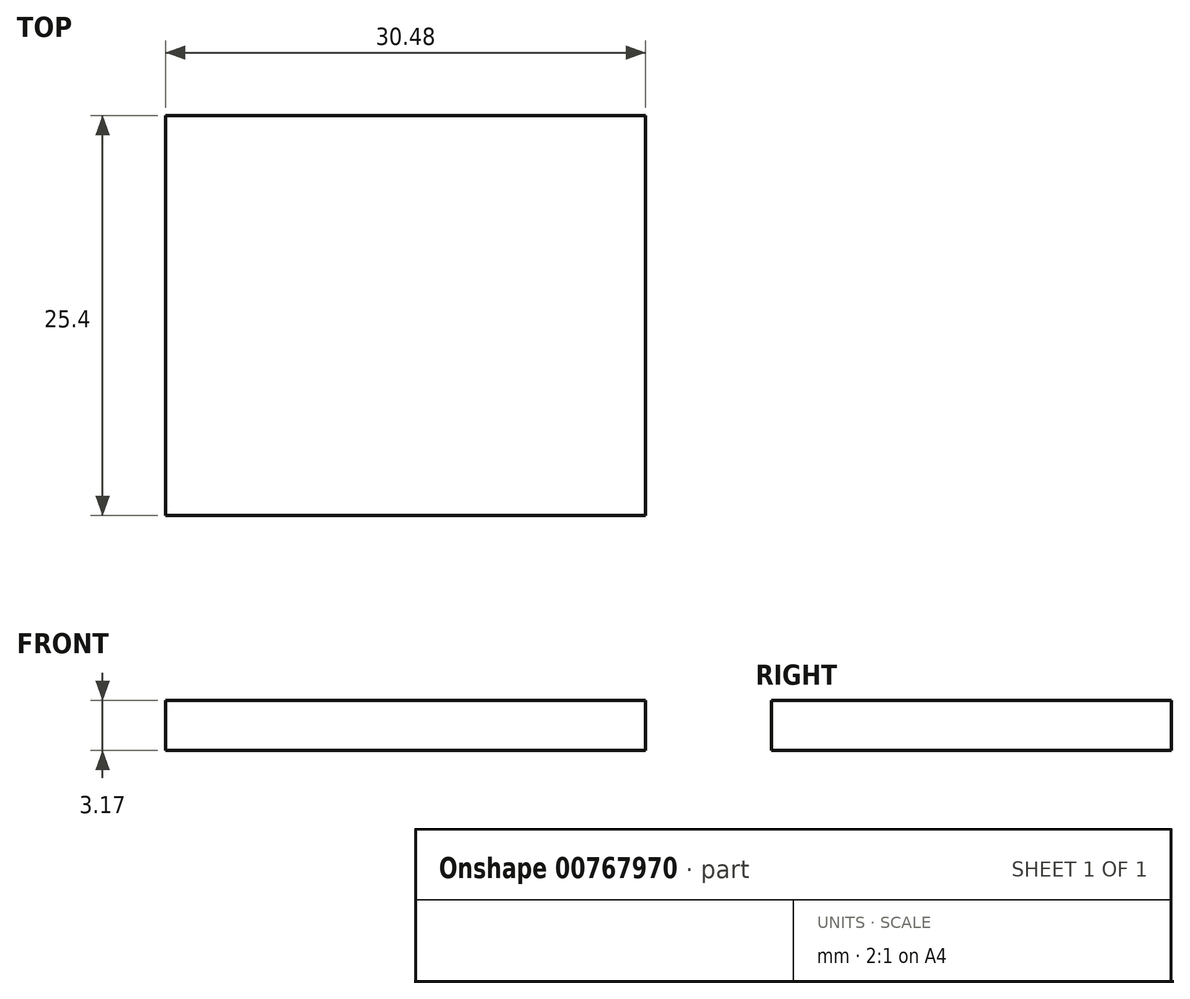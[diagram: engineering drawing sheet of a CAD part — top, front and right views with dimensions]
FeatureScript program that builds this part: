
annotation { "Feature Type Name" : "Feature", "Feature Type Description" : "" }
export const myFeature = defineFeature(function(context is Context, id is Id, definition is map)
    precondition{}
    {
        {
            var Q0;
            Q0=qCreatedBy(makeId("Top.planeOp"),FACE);
            var sketch = newSketch(context, id + "F0", { "sketchPlane" : qUnion([Q0])});
            skLineSegment(sketch, "E0.bottom", {"start": v(0.22, 0.78) * mm, "end": v(30.7, 0.78) * mm});
            skLineSegment(sketch, "E0.top", {"start": v(0.22, 26.18) * mm, "end": v(30.7, 26.18) * mm});
            skLineSegment(sketch, "E0.left", {"start": v(0.22, 0.78) * mm, "end": v(0.22, 26.18) * mm});
            skLineSegment(sketch, "E0.right", {"start": v(30.7, 0.78) * mm, "end": v(30.7, 26.18) * mm});
            skSolve(sketch);
        }
        {
            var Q0;
            Q0=makeQuery(id+"F0.imprint","IMPRINT",FACE,{"disambiguationData":[TD([[makeQuery(id+"F0.imprint","IMPRINT",EDGE,{"derivedFrom":sQuery(id+"F0.wireOp",EDGE,"E0.bottom")}),1.0]])]});
            extrude(context, id + "F1", {"entities" : qUnion([Q0]), "depth" : 3.17 * mm, "offsetDistance" : 25.4 * mm});
        }
    });
